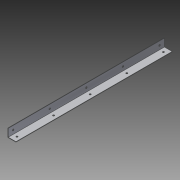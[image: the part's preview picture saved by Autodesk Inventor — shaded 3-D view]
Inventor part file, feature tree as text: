
AUTODESK INVENTOR PART (.ipt)
format: ipt  version: 2014 SP1 (Build 180222100, 222)  size: 108,032 bytes
history: native  units: in
note: dims shown in document units (in); Inventor stores cm internally (conversion verified against a paired STEP export)
features: extrude x3, sketch x3
ambient origin geometry x8: Origin, YZ Plane, XZ Plane, XY Plane, X Axis, Y Axis, Z Axis, Center Point
bodies: Solid1 (feature_tree)
feature tree (6):
  extrude  "Extrusion1"  Depth=0.0312in
  sketch  "Sketch2"  dims[d2=12.0in d3=0.0in d4=0.375in]
  sketch  "Sketch3"  dims[d5=0.125in d6=12.0in d7=1.9685in d9=2.8125in d10=0.3937in d12=1.0in d14=0.125in d15=0.375in d16=12.0in d17=1.9685in d19=2.8125in d20=0.3937in d22=1.0in d24=1.0in d25=0.0in d26=1.0in d27=0.0in]
  extrude  "Extrusion2"  Depth=12.0in
  extrude  "Extrusion3"  Depth=12.0in
  sketch  "Sketch1"  dims[d0=0.625in d1=0.0312in]
